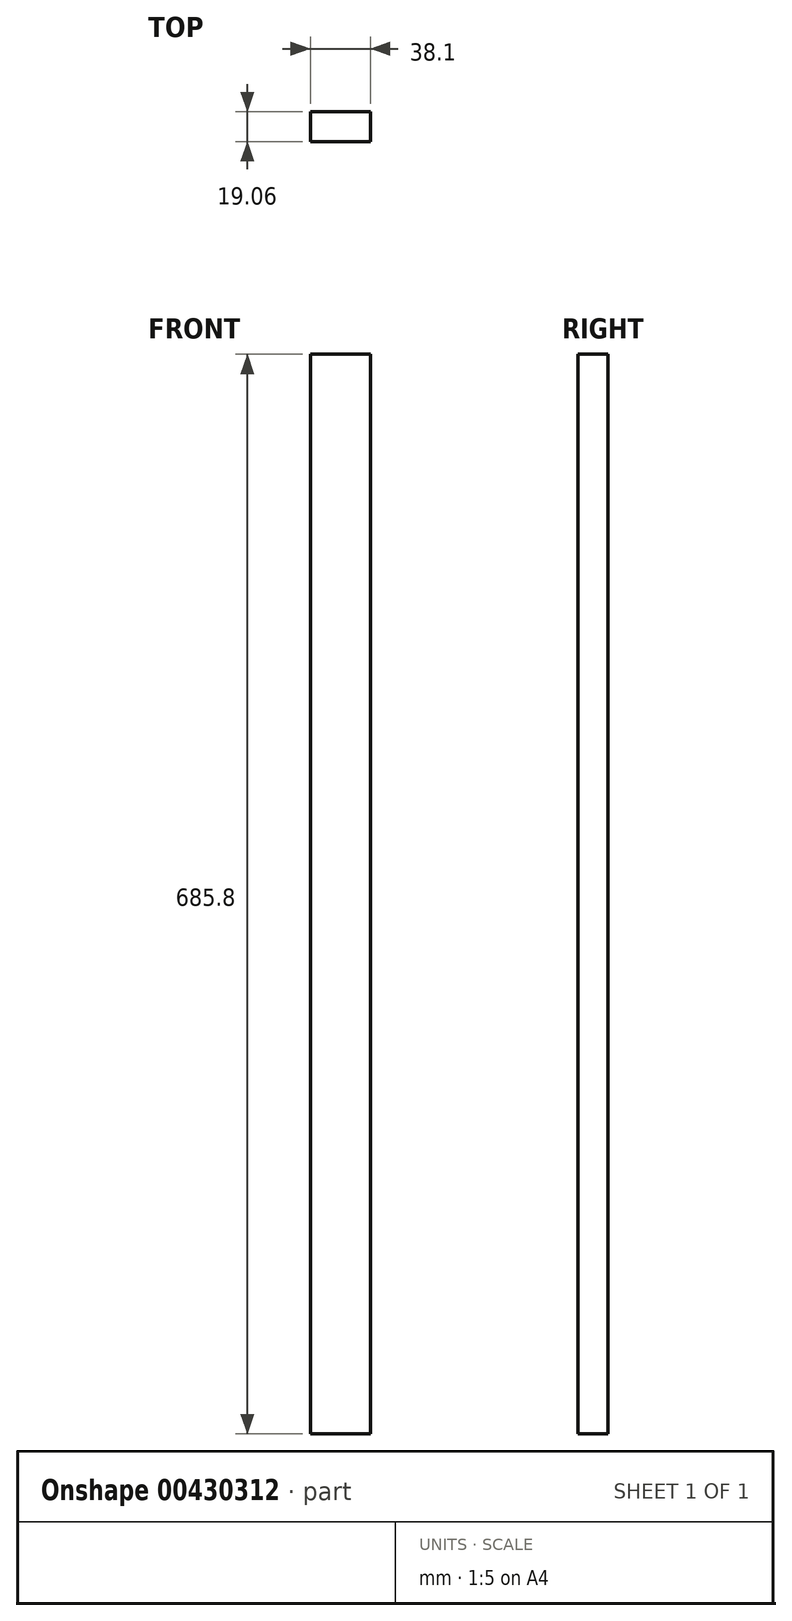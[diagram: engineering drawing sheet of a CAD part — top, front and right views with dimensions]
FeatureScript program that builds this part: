
annotation { "Feature Type Name" : "Feature", "Feature Type Description" : "" }
export const myFeature = defineFeature(function(context is Context, id is Id, definition is map)
    precondition{}
    {
        {
            var Q0;
            Q0=qCreatedBy(makeId("Top.planeOp"),FACE);
            var sketch = newSketch(context, id + "F0", { "sketchPlane" : qUnion([Q0])});
            skLineSegment(sketch, "E0.bottom", {"start": v(19.05, 9.53) * mm, "end": v(-19.05, 9.53) * mm});
            skLineSegment(sketch, "E0.top", {"start": v(19.05, -9.53) * mm, "end": v(-19.05, -9.53) * mm});
            skLineSegment(sketch, "E0.left", {"start": v(19.05, 9.53) * mm, "end": v(19.05, -9.53) * mm});
            skLineSegment(sketch, "E0.right", {"start": v(-19.05, 9.53) * mm, "end": v(-19.05, -9.53) * mm});
            skPoint(sketch, "E0.middle", {"position": v(0, 0) * mm});
            skSolve(sketch);
        }
        {
            var Q0;
            Q0 = qSketchRegion(id + "F0", true);
            extrude(context, id + "F1", {"entities" : qUnion([Q0]), "depth" : 685.8 * mm});
        }
    });
